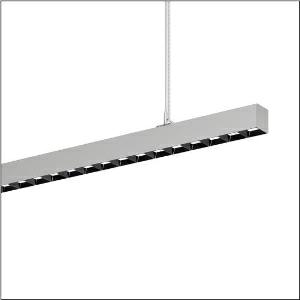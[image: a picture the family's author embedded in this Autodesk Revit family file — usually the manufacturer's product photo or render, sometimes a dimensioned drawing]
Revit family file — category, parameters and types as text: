
# Revit family: silica_r__21_51mx34dc3dsb_1a3f
name_source: partatom
category: Lighting Fixtures
units: mm (PartAtom-declared; Revit-internal decimal feet)

## family parameters
Cut with Voids When Loaded = No
Host = Face
Light Source = No
Part Type = Normal
Room Calculation Point = No
Round Connector Dimension = Use Diameter
Shared = No

## types (1)
- --- (1 x LED, 19200 lm, 129.1 W, 3000K)
    Apparent Load = 129 VA
    CIE Flux Codes = 74 94 99 56 100
    Color Rendering = 80
    Color Temperature = 3000K
    Default Elevation = 1800 mm
    Description = Silica® 21, office luminaire, primary light control with darklight reflector, of PMMA, black, light emission: direct/indirect distribution, primary light characteristic: asymmetric, installation type: suspended mounting, LED, rated luminous flux: 19.200lm, luminous efficacy: 149lm/W, light colour: 830, colour temperature: 3000K, with terminal, 3+2-pole, max. 2.5mm², mains connection: 220..240V, AC, 50/60Hz, rated input power: 129.1W, luminaire housing, of aluminium, metallic grey (RAL 9006), length: 3.004mm, width: 53mm, height: 53mm, protection rating (complete): IP20, insulation class (complete): insulation class I (protective earthing), certification: CE, permissible operating ambient temperature: 0..+35°C, standard: EN 50419, packaging unit: 1 piece
    Height = 53 mm
    Lamp = 1 x LED
    Lamp Light Flux = 19200 lm
    Lamp Power = 129.1 W
    Lamp count = 1
    Length = 3004 mm
    Luminous efficacy = 149 lm/W
    Manufacturer = Siteco
    ModVariant = No
    Model = 51MX34DC3DSB
    Mounting Place = Ceiling
    Mounting Type = Pendant
    Number of Poles = 1
    OnlyDefault = Yes
    Power Factor = 1
    Product Name = Silica® 21
    Product group = office luminaire | ceiling pendant
    ProductGroupID = 902
    Protection Class = Protection class I
    Protection Degree = IP 20
    RLX_Detail_Level = 1
    RLX_Emergency_Light_Flux = 0 lm
    RLX_Emergency_Type = 0
    RLX_Emergency_Type_DB = No
    RlxData = <blob elided: 66925 chars, md5=2551dfbf>
    Socket = socket
    Standby Power = 0 W
    System Light Flux = 19200 lm
    System Power = 129 W
    Type Comments = factory setting: luminous flux: 100 % | dim-lin: 254 | 448 mA
    Type Image = l_1297751.jpg
    URL = http://relux.com
    VarID = @adj_050537
    Voltage = 0 V
    Weight = 0.00 kg
    Width = 53 mm

## geometry (parser evidence)
native form markers: Blend x4, Sweep x12
no freeform markers — native parametric forms only
